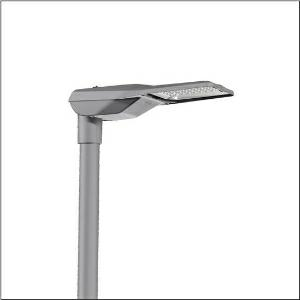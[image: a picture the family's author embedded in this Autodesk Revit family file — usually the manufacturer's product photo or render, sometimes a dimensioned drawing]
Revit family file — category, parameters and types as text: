
# Revit family: streetlight_sl_21_mini___st0_5a_5xe2b33s08gb_907c
name_source: partatom
category: Lighting Fixtures
units: mm (PartAtom-declared; Revit-internal decimal feet)

## family parameters
Cut with Voids When Loaded = No
Host = Face
Light Source = No
Part Type = Normal
Room Calculation Point = No
Round Connector Dimension = Use Diameter
Shared = No

## types (1)
- --- (1 x LED, 5940 lm, 40.4 W, 3000K)
    Apparent Load = 40 VA
    CIE Flux Codes = 41 75 97 100 100
    Color Rendering = 70
    Color Temperature = 3000K
    Default Elevation = 1800 mm
    Description = Streetlight SL 21 mini, mast luminaire, primary light control with lens, of PMMA, primary optical cover: cover, of toughened safety glass, transparent, light distribution: ST0.5a, light emission: direct distribution, primary light characteristic: asymmetric, installation type: side-entry, post-top, LED, High Power LED, rated luminous flux: 5.940lm, luminous efficacy: 147lm/W, light colour: 730, colour temperature: 3000K, control gear: ECG Smart Interface, control: overheat protection, constant luminous flux control, time-dependent luminous flux control, flexible luminous flux parameterisation, mains connection: 220..240V, AC, 50/60Hz, start of lifetime: 40W, end of lifetime: 41W, reduction: 19W, luminaire housing, of diecast aluminium, powder-coated, Siteco® metallic grey (DB 702S), corrosivity category C5 according to DIN EN ISO 12944, length: 628mm, width: 235mm, height: 110mm, spigot size: 60/76mm (post-top) and 42/60/76mm (side-entry), mast flange for spigot size: 42mm: 5XC10008XM4, 60mm: 5XC10008XM2, 76/60mm: 5XC10108XM1, protection rating (complete): IP66, insulation class (complete): insulation class II (safety insulation), certification: CE, ENEC, VDE, impact resistance: IK09, permissible operating ambient temperature for outdoor applications: -40..+50°C, standard-compliant lighting for roads and squares, packaging unit: 1 piece

Light Distribution: ST0.5a
    Height = 110 mm
    Lamp = 1 x LED
    Lamp Light Flux = 5940 lm
    Lamp Power = 40.4 W
    Lamp count = 1
    Length = 625 mm
    Luminous efficacy = 147 lm/W
    Manufacturer = Siteco
    ModVariant = No
    Model = 5XE2B33S08GB
    Number of Poles = 1
    OnlyDefault = Yes
    Power Factor = 1
    Product Name = Streetlight SL 21 mini | ST0.5a
    Product group = mast luminaire | pylon top
    ProductGroupID = 6100
    Protection Class = Protection class II
    Protection Degree = IP 66
    RLX_Detail_Level = 1
    RlxData = <blob elided: 103057 chars, md5=4edae6ae>
    Socket = socket
    Standby Power = 0 W
    System Light Flux = 5940 lm
    System Power = 40 W
    Type Comments = factory setting: luminous flux: 100 % | dim-lin: 254 | 812 mA
    Type Image = l_1003515.jpg
    URL = http://relux.com
    VarID = @adj_111225
    Voltage = 0 V
    Weight = 0.00 kg
    Width = 234 mm

## geometry (parser evidence)
native form markers: Blend x4, Sweep x8
no freeform markers — native parametric forms only
